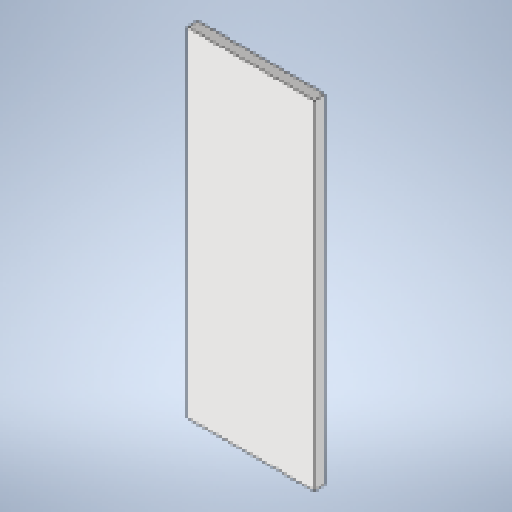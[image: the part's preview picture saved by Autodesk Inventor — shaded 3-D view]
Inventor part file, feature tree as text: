
AUTODESK INVENTOR PART (.ipt)
format: ipt  version: 2025 (Build 290162010, 162A)  size: 223,232 bytes
history: native  units: mm
features: extrude x1
ambient origin geometry x8: Origin, YZ Plane, XZ Plane, XY Plane, X Axis, Y Axis, Z Axis, Center Point
bodies: Solid1 (feature_tree)
feature tree (1):
  extrude  "Extrusion1"  Depth=1200.0mm
